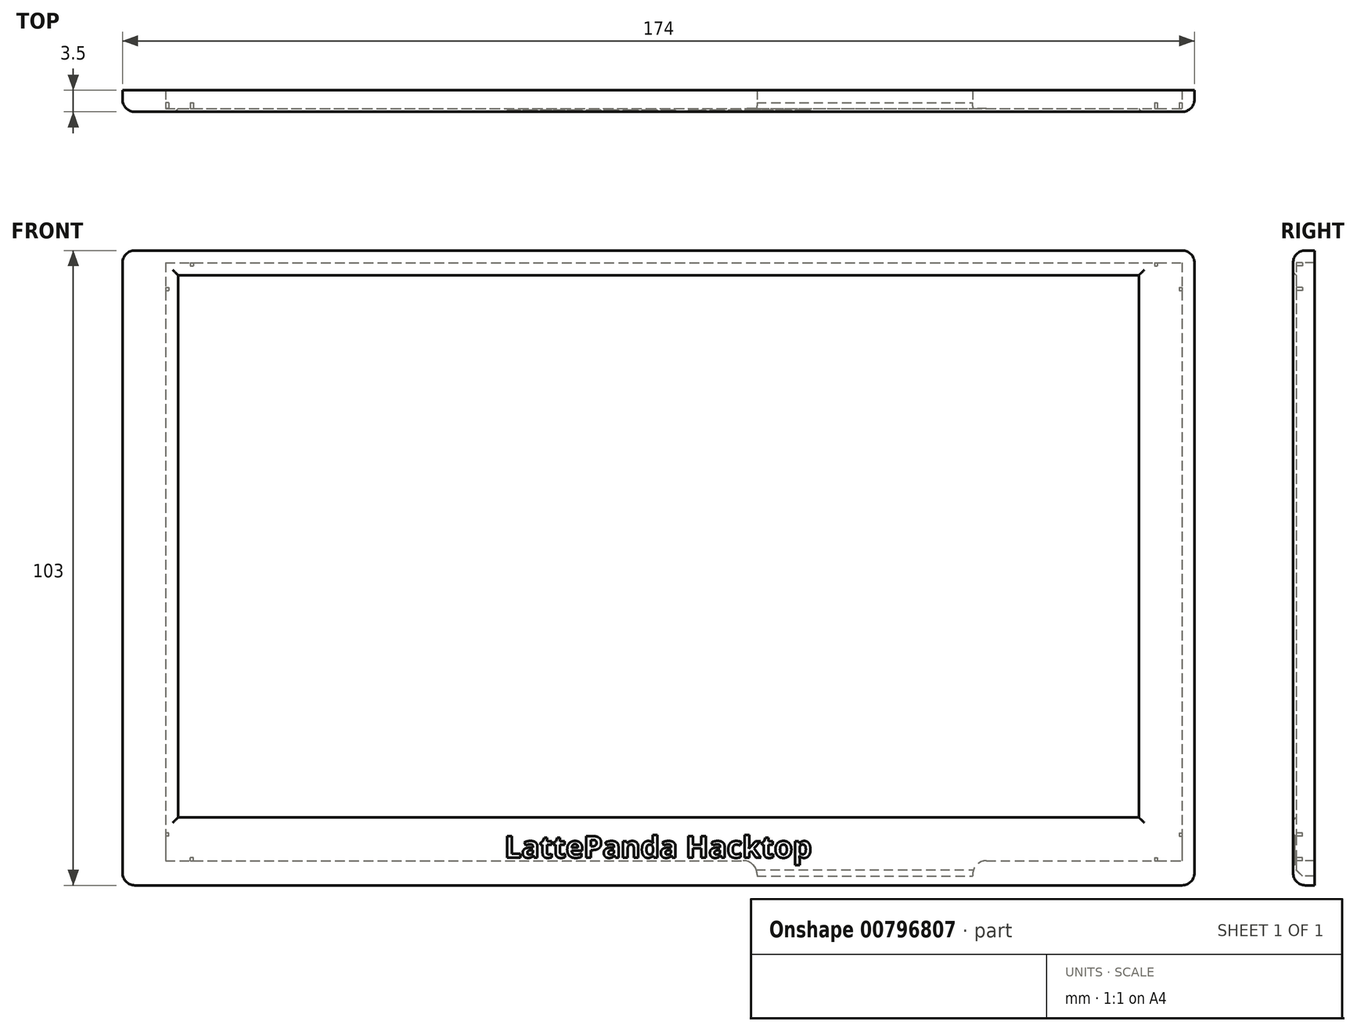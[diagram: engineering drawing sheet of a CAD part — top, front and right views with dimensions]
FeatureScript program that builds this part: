
annotation { "Feature Type Name" : "Feature", "Feature Type Description" : "" }
export const myFeature = defineFeature(function(context is Context, id is Id, definition is map)
    precondition{}
    {
        {
            var Q0;
            Q0=qCreatedBy(makeId("Front.planeOp"),FACE);
            var sketch = newSketch(context, id + "F0", { "sketchPlane" : qUnion([Q0])});
            skLineSegment(sketch, "E0.bottom", {"start": v(-82.5, 48.5) * mm, "end": v(82.5, 48.5) * mm});
            skLineSegment(sketch, "E0.top", {"start": v(-82.5, -48.5) * mm, "end": v(13.5, -48.5) * mm});
            skLineSegment(sketch, "E0.left", {"start": v(-82.5, 48.5) * mm, "end": v(-82.5, -48.5) * mm});
            skLineSegment(sketch, "E0.right", {"start": v(82.5, 48.5) * mm, "end": v(82.5, -48.5) * mm});
            skLineSegment(sketch, "E1.trimOffspring", {"start": v(48.5, -48.5) * mm, "end": v(82.5, -48.5) * mm});
            skLineSegment(sketch, "E2.bottom", {"start": v(-87.5, 50.5) * mm, "end": v(82.5, 50.5) * mm});
            skLineSegment(sketch, "E2.top", {"start": v(-87.5, -52.5) * mm, "end": v(82.5, -52.5) * mm});
            skLineSegment(sketch, "E2.left", {"start": v(-89.5, 48.5) * mm, "end": v(-89.5, -50.5) * mm});
            skLineSegment(sketch, "E2.right", {"start": v(84.5, 48.5) * mm, "end": v(84.5, -50.5) * mm});
            skLineSegment(sketch, "E3", {"start": v(13.5, -48.5) * mm, "end": v(13.5, -51) * mm});
            skLineSegment(sketch, "E4", {"start": v(13.5, -51) * mm, "end": v(48.5, -51) * mm});
            skLineSegment(sketch, "E5", {"start": v(48.5, -51) * mm, "end": v(48.5, -48.5) * mm});
            skArc(sketch, "E6", {"start": v(82.5, -52.5) * mm, "mid": v(83.91, -51.91) * mm, "end": v(84.5, -50.5) * mm});
            skArc(sketch, "E7", {"start": v(82.5, 50.5) * mm, "mid": v(83.91, 49.91) * mm, "end": v(84.5, 48.5) * mm});
            skArc(sketch, "E8", {"start": v(-89.5, 48.5) * mm, "mid": v(-88.91, 49.91) * mm, "end": v(-87.5, 50.5) * mm});
            skArc(sketch, "E9", {"start": v(-89.5, -50.5) * mm, "mid": v(-88.91, -51.91) * mm, "end": v(-87.5, -52.5) * mm});
            skLineSegment(sketch, "E10.bottom", {"start": v(-82.5, 44.5) * mm, "end": v(-82, 44.5) * mm});
            skLineSegment(sketch, "E10.top", {"start": v(-82.5, 44) * mm, "end": v(-82, 44) * mm});
            skLineSegment(sketch, "E10.left", {"start": v(-82.5, 44.5) * mm, "end": v(-82.5, 44) * mm});
            skLineSegment(sketch, "E10.right", {"start": v(-82, 44.5) * mm, "end": v(-82, 44) * mm});
            skLineSegment(sketch, "E11.bottom", {"start": v(-78.5, 48.5) * mm, "end": v(-78, 48.5) * mm});
            skLineSegment(sketch, "E11.top", {"start": v(-78.5, 48) * mm, "end": v(-78, 48) * mm});
            skLineSegment(sketch, "E11.left", {"start": v(-78.5, 48.5) * mm, "end": v(-78.5, 48) * mm});
            skLineSegment(sketch, "E11.right", {"start": v(-78, 48.5) * mm, "end": v(-78, 48) * mm});
            skLineSegment(sketch, "E12.bottom", {"start": v(-82, -44.5) * mm, "end": v(-82.5, -44.5) * mm});
            skLineSegment(sketch, "E12.top", {"start": v(-82, -44) * mm, "end": v(-82.5, -44) * mm});
            skLineSegment(sketch, "E12.left", {"start": v(-82, -44.5) * mm, "end": v(-82, -44) * mm});
            skLineSegment(sketch, "E12.right", {"start": v(-82.5, -44.5) * mm, "end": v(-82.5, -44) * mm});
            skLineSegment(sketch, "E13.bottom", {"start": v(-78, -48.5) * mm, "end": v(-78.5, -48.5) * mm});
            skLineSegment(sketch, "E13.top", {"start": v(-78, -48) * mm, "end": v(-78.5, -48) * mm});
            skLineSegment(sketch, "E13.left", {"start": v(-78, -48.5) * mm, "end": v(-78, -48) * mm});
            skLineSegment(sketch, "E13.right", {"start": v(-78.5, -48.5) * mm, "end": v(-78.5, -48) * mm});
            skLineSegment(sketch, "E14.bottom", {"start": v(78, 48.5) * mm, "end": v(78.5, 48.5) * mm});
            skLineSegment(sketch, "E14.top", {"start": v(78, 48) * mm, "end": v(78.5, 48) * mm});
            skLineSegment(sketch, "E14.left", {"start": v(78, 48.5) * mm, "end": v(78, 48) * mm});
            skLineSegment(sketch, "E14.right", {"start": v(78.5, 48.5) * mm, "end": v(78.5, 48) * mm});
            skLineSegment(sketch, "E15.bottom", {"start": v(82, 44.5) * mm, "end": v(82.5, 44.5) * mm});
            skLineSegment(sketch, "E15.top", {"start": v(82, 44) * mm, "end": v(82.5, 44) * mm});
            skLineSegment(sketch, "E15.left", {"start": v(82, 44.5) * mm, "end": v(82, 44) * mm});
            skLineSegment(sketch, "E15.right", {"start": v(82.5, 44.5) * mm, "end": v(82.5, 44) * mm});
            skLineSegment(sketch, "E16.bottom", {"start": v(82, -44) * mm, "end": v(82.5, -44) * mm});
            skLineSegment(sketch, "E16.top", {"start": v(82, -44.5) * mm, "end": v(82.5, -44.5) * mm});
            skLineSegment(sketch, "E16.left", {"start": v(82, -44) * mm, "end": v(82, -44.5) * mm});
            skLineSegment(sketch, "E16.right", {"start": v(82.5, -44) * mm, "end": v(82.5, -44.5) * mm});
            skLineSegment(sketch, "E17.bottom", {"start": v(78, -48) * mm, "end": v(78.5, -48) * mm});
            skLineSegment(sketch, "E17.top", {"start": v(78, -48.5) * mm, "end": v(78.5, -48.5) * mm});
            skLineSegment(sketch, "E17.left", {"start": v(78, -48) * mm, "end": v(78, -48.5) * mm});
            skLineSegment(sketch, "E17.right", {"start": v(78.5, -48) * mm, "end": v(78.5, -48.5) * mm});
            skLineSegment(sketch, "E18", {"start": v(13.5, -48.5) * mm, "end": v(48.5, -48.5) * mm});
            skLineSegment(sketch, "E19.bottom", {"start": v(-80.5, 46.5) * mm, "end": v(75.5, 46.5) * mm});
            skLineSegment(sketch, "E19.top", {"start": v(-80.5, -41.5) * mm, "end": v(75.5, -41.5) * mm});
            skLineSegment(sketch, "E19.left", {"start": v(-80.5, 46.5) * mm, "end": v(-80.5, -41.5) * mm});
            skLineSegment(sketch, "E19.right", {"start": v(75.5, 46.5) * mm, "end": v(75.5, -41.5) * mm});
            skSolve(sketch);
        }
        {
            var Q0;
            {var subQ24=sQuery(id+"F0.wireOp",EDGE,"E10.bottom");Q0=makeQuery(id+"F0.imprint","IMPRINT",FACE,{"disambiguationData":[TD([[makeQuery(id+"F0.imprint","IMPRINT",EDGE,{"derivedFrom":subQ24}),1.0]])]});}
            extrude(context, id + "F1", {"entities" : qUnion([Q0]), "oppositeDirection" : true, "depth" : 0.5 * mm, "offsetDistance" : 25 * mm});
        }
        {
            var Q0;
            {var subQ2=sQuery(id+"F0.wireOp",EDGE,"E10.bottom");Q0=makeQuery(id+"F0.imprint","IMPRINT",FACE,{"disambiguationData":[TD([[makeQuery(id+"F0.imprint","IMPRINT",EDGE,{"derivedFrom":subQ2}),-1.0]])]});}
            var Q1;
            Q1=makeQuery(id+"F0.imprint","IMPRINT",FACE,{"disambiguationData":[TD([[makeQuery(id+"F0.imprint","IMPRINT",EDGE,{"derivedFrom":sQuery(id+"F0.wireOp",EDGE,"E11.top")}),1.0]])]});
            var Q2;
            {var subQ0=sQuery(id+"F0.wireOp",EDGE,"E12.bottom");Q2=makeQuery(id+"F0.imprint","IMPRINT",FACE,{"disambiguationData":[TD([[makeQuery(id+"F0.imprint","IMPRINT",EDGE,{"derivedFrom":subQ0}),-1.0]])]});}
            var Q3;
            Q3=makeQuery(id+"F0.imprint","IMPRINT",FACE,{"disambiguationData":[TD([[makeQuery(id+"F0.imprint","IMPRINT",EDGE,{"derivedFrom":sQuery(id+"F0.wireOp",EDGE,"E13.top")}),1.0]])]});
            var Q4;
            Q4=makeQuery(id+"F0.imprint","IMPRINT",FACE,{"disambiguationData":[TD([[makeQuery(id+"F0.imprint","IMPRINT",EDGE,{"derivedFrom":sQuery(id+"F0.wireOp",EDGE,"E17.bottom")}),-1.0]])]});
            var Q5;
            {var subQ2=sQuery(id+"F0.wireOp",EDGE,"E16.bottom");Q5=makeQuery(id+"F0.imprint","IMPRINT",FACE,{"disambiguationData":[TD([[makeQuery(id+"F0.imprint","IMPRINT",EDGE,{"derivedFrom":subQ2}),-1.0]])]});}
            var Q6;
            Q6=makeQuery(id+"F0.imprint","IMPRINT",FACE,{"disambiguationData":[TD([[makeQuery(id+"F0.imprint","IMPRINT",EDGE,{"derivedFrom":sQuery(id+"F0.wireOp",EDGE,"E14.top")}),1.0]])]});
            var Q7;
            {var subQ2=sQuery(id+"F0.wireOp",EDGE,"E15.bottom");Q7=makeQuery(id+"F0.imprint","IMPRINT",FACE,{"disambiguationData":[TD([[makeQuery(id+"F0.imprint","IMPRINT",EDGE,{"derivedFrom":subQ2}),-1.0]])]});}
            extrude(context, id + "F2", {"entities" : qUnion([Q0, Q1, Q2, Q3, Q4, Q5, Q6, Q7]), "operationType" : NewBodyOperationType.ADD, "oppositeDirection" : true, "depth" : 1.5 * mm, "offsetDistance" : 25 * mm});
        }
        {
            var Q0;
            Q0=makeQuery(id+"F0.imprint","IMPRINT",FACE,{"disambiguationData":[TD([[makeQuery(id+"F0.imprint","IMPRINT",EDGE,{"derivedFrom":sQuery(id+"F0.wireOp",EDGE,"E3")}),1.0]])]});
            extrude(context, id + "F3", {"entities" : qUnion([Q0]), "operationType" : NewBodyOperationType.ADD, "oppositeDirection" : true, "depth" : 1.5 * mm, "offsetDistance" : 25 * mm});
        }
        {
            var Q0;
            Q0=makeQuery(id+"F0.imprint","IMPRINT",FACE,{"disambiguationData":[TD([[makeQuery(id+"F0.imprint","IMPRINT",EDGE,{"derivedFrom":sQuery(id+"F0.wireOp",EDGE,"E2.bottom")}),-1.0]])]});
            extrude(context, id + "F4", {"entities" : qUnion([Q0]), "operationType" : NewBodyOperationType.ADD, "oppositeDirection" : true, "depth" : 3.5 * mm, "offsetDistance" : 25 * mm});
        }
        {
            var Q0;
            Q0=makeQuery(id+"F4.opExtrude","CAP_EDGE",EDGE,{"disambiguationData":[OSD([sQuery(id+"F0.wireOp",EDGE,"E2.bottom")])],"isStart":true});
            var Q1;
            Q1=makeQuery(id+"F4.opExtrude","CAP_EDGE",EDGE,{"disambiguationData":[OSD([sQuery(id+"F0.wireOp",EDGE,"E8")])],"isStart":true});
            var Q2;
            Q2=makeQuery(id+"F4.opExtrude","CAP_EDGE",EDGE,{"disambiguationData":[OSD([sQuery(id+"F0.wireOp",EDGE,"E2.left")])],"isStart":true});
            var Q3;
            Q3=makeQuery(id+"F4.opExtrude","CAP_EDGE",EDGE,{"disambiguationData":[OSD([sQuery(id+"F0.wireOp",EDGE,"E9")])],"isStart":true});
            var Q4;
            Q4=makeQuery(id+"F4.opExtrude","CAP_EDGE",EDGE,{"disambiguationData":[OSD([sQuery(id+"F0.wireOp",EDGE,"E2.top")])],"isStart":true});
            var Q5;
            Q5=makeQuery(id+"F4.opExtrude","CAP_EDGE",EDGE,{"disambiguationData":[OSD([sQuery(id+"F0.wireOp",EDGE,"E6")])],"isStart":true});
            var Q6;
            Q6=makeQuery(id+"F4.opExtrude","CAP_EDGE",EDGE,{"disambiguationData":[OSD([sQuery(id+"F0.wireOp",EDGE,"E2.right")])],"isStart":true});
            var Q7;
            Q7=makeQuery(id+"F4.opExtrude","CAP_EDGE",EDGE,{"disambiguationData":[OSD([sQuery(id+"F0.wireOp",EDGE,"E7")])],"isStart":true});
            fillet(context, id + "F5", {"entities" : qUnion([Q0, Q1, Q2, Q3, Q4, Q5, Q6, Q7]), "radius" : 2 * mm, "tangentPropagation" : true, "allowEdgeOverflow" : false});
        }
        {
            var Q0;
            Q0=makeQuery(id+"F1.opExtrude","CAP_EDGE",EDGE,{"disambiguationData":[OSD([sQuery(id+"F0.wireOp",EDGE,"E19.top")])],"isStart":true});
            var Q1;
            Q1=makeQuery(id+"F1.opExtrude","CAP_EDGE",EDGE,{"disambiguationData":[OSD([sQuery(id+"F0.wireOp",EDGE,"E19.right")])],"isStart":true});
            var Q2;
            Q2=makeQuery(id+"F1.opExtrude","CAP_EDGE",EDGE,{"disambiguationData":[OSD([sQuery(id+"F0.wireOp",EDGE,"E19.bottom")])],"isStart":true});
            var Q3;
            Q3=makeQuery(id+"F1.opExtrude","CAP_EDGE",EDGE,{"disambiguationData":[OSD([sQuery(id+"F0.wireOp",EDGE,"E19.left")])],"isStart":true});
            fillet(context, id + "F6", {"entities" : qUnion([Q0, Q1, Q2, Q3]), "radius" : 1 * mm, "tangentPropagation" : true, "allowEdgeOverflow" : false});
        }
        {
            var Q0;
            Q0=makeQuery(id+"F3.opExtrude","CAP_EDGE",EDGE,{"disambiguationData":[OSD([sQuery(id+"F0.wireOp",EDGE,"E18")])],"isStart":false});
            chamfer(context, id + "F7", {"entities" : qUnion([Q0]), "width" : 2.5 * mm, "tangentPropagation" : true});
        }
        {
            var Q0;
            Q0=makeQuery(id+"F4.opExtrude","SWEPT_EDGE",EDGE,{"disambiguationData":[OSD([sQuery(id+"F0.wireOp",EDGE,"E1.trimOffspring"),sQuery(id+"F0.wireOp",EDGE,"E5"),sQuery(id+"F0.wireOp",EDGE,"E18")])]});
            var Q1;
            Q1=makeQuery(id+"F4.opExtrude","SWEPT_EDGE",EDGE,{"disambiguationData":[OSD([sQuery(id+"F0.wireOp",EDGE,"E0.top"),sQuery(id+"F0.wireOp",EDGE,"E3"),sQuery(id+"F0.wireOp",EDGE,"E18")])]});
            fillet(context, id + "F8", {"entities" : qUnion([Q0, Q1]), "radius" : 2.25 * mm, "tangentPropagation" : true, "allowEdgeOverflow" : false});
        }
        {
            var Q0;
            Q0=qCreatedBy(makeId("Front.planeOp"),FACE);
            var sketch = newSketch(context, id + "F9", { "sketchPlane" : qUnion([Q0])});
            skText(sketch, "E20", { "text": "LattePanda Hacktop", "fontName": "NotoSans-Bold.ttf"});
            const initialGuessF9  = {"E20": [-0.0275, -0.04802, 1, 0, 0.00352]};
            skSetInitialGuess(sketch, initialGuessF9);
            skSolve(sketch);
        }
        {
            var Q0;
            Q0 = qSketchRegion(id + "F9", true);
            extrude(context, id + "F10", {"entities" : qUnion([Q0]), "operationType" : NewBodyOperationType.REMOVE, "oppositeDirection" : true, "depth" : 0.25 * mm, "offsetDistance" : 25 * mm});
        }
    });
